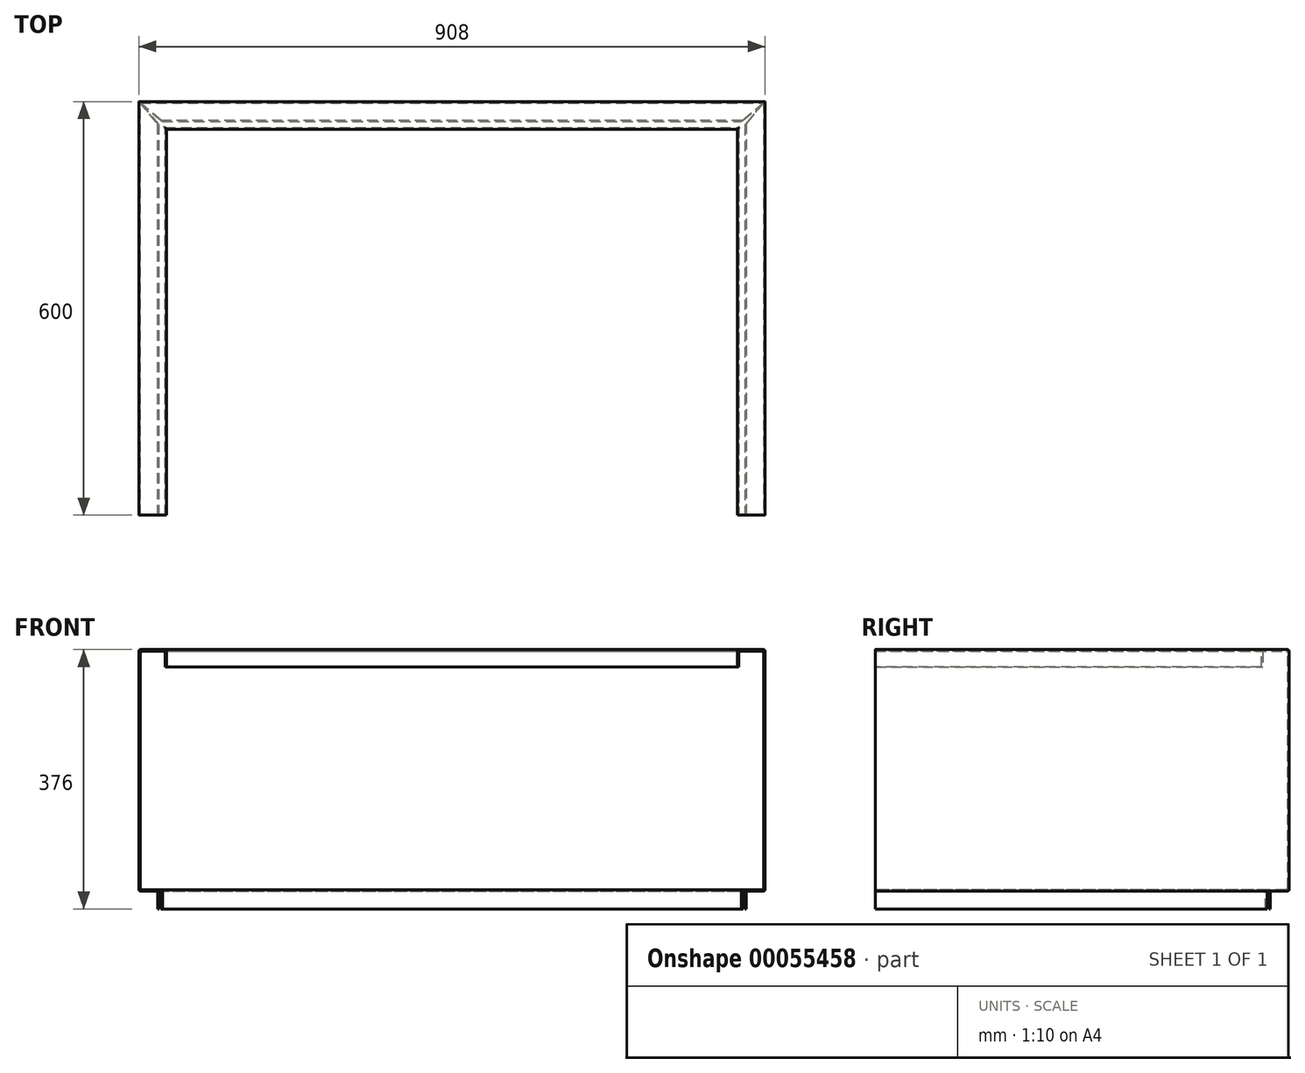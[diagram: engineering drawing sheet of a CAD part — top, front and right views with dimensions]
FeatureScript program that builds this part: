
annotation { "Feature Type Name" : "Feature", "Feature Type Description" : "" }
export const myFeature = defineFeature(function(context is Context, id is Id, definition is map)
    precondition{}
    {
        {
            var Q0;
            Q0=qCreatedBy(makeId("Front.planeOp"),FACE);
            var sketch = newSketch(context, id + "F0", { "sketchPlane" : qUnion([Q0])});
            skLineSegment(sketch, "E0", {"start": v(40, -25) * mm, "end": v(40, 0) * mm});
            skLineSegment(sketch, "E1", {"start": v(40, 0) * mm, "end": v(0, 0) * mm});
            skLineSegment(sketch, "E2", {"start": v(0, 0) * mm, "end": v(0, -350) * mm});
            skLineSegment(sketch, "E3", {"start": v(0, -350) * mm, "end": v(27, -350) * mm});
            skLineSegment(sketch, "E4", {"start": v(27, -350) * mm, "end": v(27, -376) * mm});
            skLineSegment(sketch, "E5.0", {"start": v(29, -348) * mm, "end": v(29, -376) * mm});
            skLineSegment(sketch, "E5.1", {"start": v(38, -25) * mm, "end": v(38, -2) * mm});
            skLineSegment(sketch, "E5.2", {"start": v(38, -2) * mm, "end": v(2, -2) * mm});
            skLineSegment(sketch, "E5.3", {"start": v(2, -2) * mm, "end": v(2, -348) * mm});
            skLineSegment(sketch, "E5.4", {"start": v(2, -348) * mm, "end": v(29, -348) * mm});
            skLineSegment(sketch, "E6", {"start": v(38, -25) * mm, "end": v(40, -25) * mm});
            skLineSegment(sketch, "E7", {"start": v(27, -376) * mm, "end": v(29, -376) * mm});
            skSolve(sketch);
        }
        {
            var Q0;
            Q0=qCreatedBy(makeId("Top.planeOp"),FACE);
            var sketch = newSketch(context, id + "F1", { "sketchPlane" : qUnion([Q0])});
            skLineSegment(sketch, "E8", {"start": v(0, 0) * mm, "end": v(0, 600) * mm});
            skLineSegment(sketch, "E9", {"start": v(0, 600) * mm, "end": v(908, 600) * mm});
            skLineSegment(sketch, "E10", {"start": v(908, 600) * mm, "end": v(908, 0) * mm});
            skSolve(sketch);
        }
        {
            var Q0;
            Q0=qSketchRegion(id+"F0",true);
            var Q1;
            Q1=qConstructionFilter(qBodyType(qCreatedBy(id+"F1",EDGE),BodyType.WIRE),ConstructionObject.NO);
            sweep(context, id + "F2", {"profiles" : qUnion([Q0]), "path" : qUnion([Q1])});
        }
        {
            var Q0;
            Q0=makeQuery(id+"F2.opSweep","SWEPT_FACE",FACE,{"disambiguationData":[OSD([sQuery(id+"F0.wireOp",EDGE,"E5.4"),sQuery(id+"F1.wireOp",EDGE,"E8")])]});
            var sketch = newSketch(context, id + "F3", { "sketchPlane" : qUnion([Q0])});
            skLineSegment(sketch, "E11", {"start": v(2, 598) * mm, "end": v(29, 565.82) * mm});
            skLineSegment(sketch, "E12", {"start": v(29, 565.82) * mm, "end": v(34.18, 571) * mm});
            skLineSegment(sketch, "E13", {"start": v(34.18, 571) * mm, "end": v(2, 598) * mm});
            skLineSegment(sketch, "E14", {"start": v(906, 598) * mm, "end": v(879, 565.82) * mm});
            skLineSegment(sketch, "E15", {"start": v(879, 565.82) * mm, "end": v(873.82, 571) * mm});
            skLineSegment(sketch, "E16", {"start": v(873.82, 571) * mm, "end": v(906, 598) * mm});
            skSolve(sketch);
        }
        {
            var Q0;
            {var subQ0=sQuery(id+"F3.wireOp",EDGE,"E14");Q0=makeQuery(id+"F3.imprint","IMPRINT",FACE,{"disambiguationData":[TD([[makeQuery(id+"F3.imprint","IMPRINT",EDGE,{"derivedFrom":subQ0}),-1.0]])]});}
            var Q1;
            {var subQ0=sQuery(id+"F3.wireOp",EDGE,"E11");Q1=makeQuery(id+"F3.imprint","IMPRINT",FACE,{"disambiguationData":[TD([[makeQuery(id+"F3.imprint","IMPRINT",EDGE,{"derivedFrom":subQ0}),1.0]])]});}
            extrude(context, id + "F4", {"entities" : qUnion([Q0, Q1]), "operationType" : NewBodyOperationType.REMOVE, "oppositeDirection" : true, "depth" : 30 * mm});
        }
        {
            var Q0;
            Q0=makeQuery(id+"F2.opSweep","SWEPT_EDGE",EDGE,{"disambiguationData":[OSD([sQuery(id+"F0.wireOp",EDGE,"E1"),sQuery(id+"F0.wireOp",EDGE,"E2"),sQuery(id+"F1.wireOp",EDGE,"E8")])]});
            var Q1;
            Q1=makeQuery(id+"F2.opSweep","SWEPT_EDGE",EDGE,{"disambiguationData":[OSD([sQuery(id+"F0.wireOp",EDGE,"E0"),sQuery(id+"F0.wireOp",EDGE,"E1"),sQuery(id+"F1.wireOp",EDGE,"E9")])]});
            var Q2;
            Q2=makeQuery(id+"F2.opSweep","SWEPT_EDGE",EDGE,{"disambiguationData":[OSD([sQuery(id+"F0.wireOp",EDGE,"E1"),sQuery(id+"F0.wireOp",EDGE,"E2"),sQuery(id+"F1.wireOp",EDGE,"E9")])]});
            var Q3;
            Q3=makeQuery(id+"F2.opSweep","SWEPT_EDGE",EDGE,{"disambiguationData":[OSD([sQuery(id+"F0.wireOp",EDGE,"E0"),sQuery(id+"F0.wireOp",EDGE,"E1"),sQuery(id+"F1.wireOp",EDGE,"E8")])]});
            var Q4;
            Q4=makeQuery(id+"F2.opSweep","SWEPT_EDGE",EDGE,{"disambiguationData":[OSD([sQuery(id+"F0.wireOp",EDGE,"E1"),sQuery(id+"F0.wireOp",EDGE,"E2"),sQuery(id+"F1.wireOp",EDGE,"E10")])]});
            var Q5;
            Q5=makeQuery(id+"F2.opSweep","SWEPT_EDGE",EDGE,{"disambiguationData":[OSD([sQuery(id+"F0.wireOp",EDGE,"E0"),sQuery(id+"F0.wireOp",EDGE,"E1"),sQuery(id+"F1.wireOp",EDGE,"E10")])]});
            var Q6;
            Q6=makeQuery(id+"F2.opSweep","SWEPT_EDGE",EDGE,{"disambiguationData":[OSD([sQuery(id+"F0.wireOp",EDGE,"E2"),sQuery(id+"F0.wireOp",EDGE,"E3"),sQuery(id+"F1.wireOp",EDGE,"E10")])]});
            var Q7;
            Q7=makeQuery(id+"F2.opSweep","SWEPT_EDGE",EDGE,{"disambiguationData":[OSD([sQuery(id+"F0.wireOp",EDGE,"E5.3"),sQuery(id+"F0.wireOp",EDGE,"E5.4"),sQuery(id+"F1.wireOp",EDGE,"E8")])]});
            var Q8;
            Q8=makeQuery(id+"F2.opSweep","SWEPT_EDGE",EDGE,{"disambiguationData":[OSD([sQuery(id+"F0.wireOp",EDGE,"E5.0"),sQuery(id+"F0.wireOp",EDGE,"E5.4"),sQuery(id+"F1.wireOp",EDGE,"E8")])]});
            var Q9;
            Q9=makeQuery(id+"F2.opSweep","SWEPT_EDGE",EDGE,{"disambiguationData":[OSD([sQuery(id+"F0.wireOp",EDGE,"E5.3"),sQuery(id+"F0.wireOp",EDGE,"E5.4"),sQuery(id+"F1.wireOp",EDGE,"E9")])]});
            var Q10;
            Q10=makeQuery(id+"F2.opSweep","SWEPT_EDGE",EDGE,{"disambiguationData":[OSD([sQuery(id+"F0.wireOp",EDGE,"E5.0"),sQuery(id+"F0.wireOp",EDGE,"E5.4"),sQuery(id+"F1.wireOp",EDGE,"E9")])]});
            var Q11;
            Q11=makeQuery(id+"F2.opSweep","SWEPT_EDGE",EDGE,{"disambiguationData":[OSD([sQuery(id+"F0.wireOp",EDGE,"E5.0"),sQuery(id+"F0.wireOp",EDGE,"E5.4"),sQuery(id+"F1.wireOp",EDGE,"E10")])]});
            var Q12;
            Q12=makeQuery(id+"F2.opSweep","SWEPT_EDGE",EDGE,{"disambiguationData":[OSD([sQuery(id+"F0.wireOp",EDGE,"E5.3"),sQuery(id+"F0.wireOp",EDGE,"E5.4"),sQuery(id+"F1.wireOp",EDGE,"E10")])]});
            var Q13;
            Q13=makeQuery(id+"F2.opSweep","SWEPT_EDGE",EDGE,{"disambiguationData":[OSD([sQuery(id+"F0.wireOp",EDGE,"E2"),sQuery(id+"F0.wireOp",EDGE,"E3"),sQuery(id+"F1.wireOp",EDGE,"E8")])]});
            var Q14;
            Q14=makeQuery(id+"F2.opSweep","SWEPT_EDGE",EDGE,{"disambiguationData":[OSD([sQuery(id+"F0.wireOp",EDGE,"E2"),sQuery(id+"F0.wireOp",EDGE,"E3"),sQuery(id+"F1.wireOp",EDGE,"E9")])]});
            var Q15;
            Q15=makeQuery(id+"F2.opSweep","SWEPT_EDGE",EDGE,{"disambiguationData":[OSD([sQuery(id+"F0.wireOp",EDGE,"E3"),sQuery(id+"F0.wireOp",EDGE,"E4"),sQuery(id+"F1.wireOp",EDGE,"E9")])]});
            var Q16;
            Q16=makeQuery(id+"F2.opSweep","SWEPT_EDGE",EDGE,{"disambiguationData":[OSD([sQuery(id+"F0.wireOp",EDGE,"E3"),sQuery(id+"F0.wireOp",EDGE,"E4"),sQuery(id+"F1.wireOp",EDGE,"E8")])]});
            var Q17;
            Q17=makeQuery(id+"F2.opSweep","SWEPT_EDGE",EDGE,{"disambiguationData":[OSD([sQuery(id+"F0.wireOp",EDGE,"E3"),sQuery(id+"F0.wireOp",EDGE,"E4"),sQuery(id+"F1.wireOp",EDGE,"E10")])]});
            var Q18;
            Q18=makeQuery(id+"F2.opSweep","SWEPT_EDGE",EDGE,{"disambiguationData":[OSD([sQuery(id+"F0.wireOp",EDGE,"E5.1"),sQuery(id+"F0.wireOp",EDGE,"E5.2"),sQuery(id+"F1.wireOp",EDGE,"E9")])]});
            var Q19;
            Q19=makeQuery(id+"F2.opSweep","SWEPT_EDGE",EDGE,{"disambiguationData":[OSD([sQuery(id+"F0.wireOp",EDGE,"E5.2"),sQuery(id+"F0.wireOp",EDGE,"E5.3"),sQuery(id+"F1.wireOp",EDGE,"E10")])]});
            var Q20;
            Q20=makeQuery(id+"F2.opSweep","SWEPT_EDGE",EDGE,{"disambiguationData":[OSD([sQuery(id+"F0.wireOp",EDGE,"E5.2"),sQuery(id+"F0.wireOp",EDGE,"E5.3"),sQuery(id+"F1.wireOp",EDGE,"E8")])]});
            var Q21;
            Q21=makeQuery(id+"F2.opSweep","SWEPT_EDGE",EDGE,{"disambiguationData":[OSD([sQuery(id+"F0.wireOp",EDGE,"E5.2"),sQuery(id+"F0.wireOp",EDGE,"E5.3"),sQuery(id+"F1.wireOp",EDGE,"E9")])]});
            var Q22;
            Q22=makeQuery(id+"F2.opSweep","SWEPT_EDGE",EDGE,{"disambiguationData":[OSD([sQuery(id+"F0.wireOp",EDGE,"E5.1"),sQuery(id+"F0.wireOp",EDGE,"E5.2"),sQuery(id+"F1.wireOp",EDGE,"E8")])]});
            fillet(context, id + "F5", {"entities" : qUnion([Q0, Q1, Q2, Q3, Q4, Q5, Q6, Q7, Q8, Q9, Q10, Q11, Q12, Q13, Q14, Q15, Q16, Q17, Q18, Q19, Q20, Q21, Q22]), "radius" : 2 * mm, "tangentPropagation" : true, "allowEdgeOverflow" : false});
        }
    });
